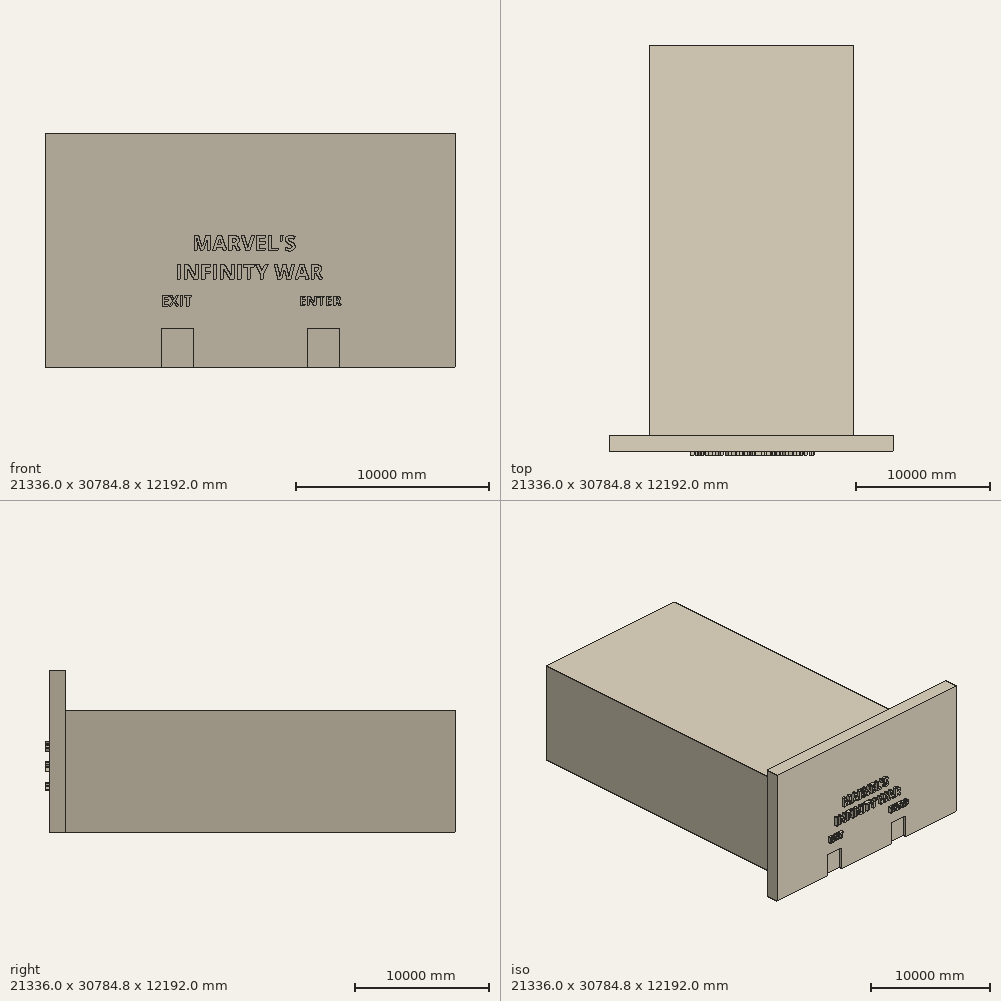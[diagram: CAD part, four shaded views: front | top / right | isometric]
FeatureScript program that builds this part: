
annotation { "Feature Type Name" : "Feature", "Feature Type Description" : "" }
export const myFeature = defineFeature(function(context is Context, id is Id, definition is map)
    precondition{}
    {
        {
            var Q0;
            Q0=qCreatedBy(makeId("Front.planeOp"),FACE);
            var sketch = newSketch(context, id + "F0", { "sketchPlane" : qUnion([Q0])});
            skLineSegment(sketch, "E0.bottom", {"start": v(-53.37, 9088.4) * mm, "end": v(15186.63, 9088.4) * mm});
            skLineSegment(sketch, "E0.top", {"start": v(-53.37, -55.6) * mm, "end": v(15186.63, -55.6) * mm});
            skLineSegment(sketch, "E0.left", {"start": v(-53.37, 9088.4) * mm, "end": v(-53.37, -55.6) * mm});
            skLineSegment(sketch, "E0.right", {"start": v(15186.63, 9088.4) * mm, "end": v(15186.63, -55.6) * mm});
            skSolve(sketch);
        }
        {
            var Q0;
            Q0=makeQuery(id+"F0.imprint","IMPRINT",FACE,{"disambiguationData":[TD([[makeQuery(id+"F0.imprint","IMPRINT",EDGE,{"derivedFrom":sQuery(id+"F0.wireOp",EDGE,"E0.bottom")}),-1.0]])]});
            extrude(context, id + "F1", {"entities" : qUnion([Q0]), "depth" : 30480 * mm, "offsetDistance" : 25 * mm});
        }
        {
            var Q0;
            Q0=makeQuery(id+"F1.opExtrude","SWEPT_FACE",FACE,{"disambiguationData":[OSD([sQuery(id+"F0.wireOp",EDGE,"E0.bottom")])]});
            var sketch = newSketch(context, id + "F2", { "sketchPlane" : qUnion([Q0])});
            skLineSegment(sketch, "E1.bottom", {"start": v(-53.37, -30480) * mm, "end": v(15186.63, -30480) * mm});
            skLineSegment(sketch, "E1.top", {"start": v(-53.37, -29276.97) * mm, "end": v(15186.63, -29276.97) * mm});
            skLineSegment(sketch, "E1.left", {"start": v(-53.37, -30480) * mm, "end": v(-53.37, -29276.97) * mm});
            skLineSegment(sketch, "E1.right", {"start": v(15186.63, -30480) * mm, "end": v(15186.63, -29276.97) * mm});
            skSolve(sketch);
        }
        {
            var Q0;
            Q0=makeQuery(id+"F2.imprint","IMPRINT",FACE,{"disambiguationData":[TD([[makeQuery(id+"F2.imprint","IMPRINT",EDGE,{"derivedFrom":sQuery(id+"F2.wireOp",EDGE,"E1.bottom")}),1.0]])]});
            extrude(context, id + "F3", {"entities" : qUnion([Q0]), "operationType" : NewBodyOperationType.ADD, "depth" : 3048 * mm, "offsetDistance" : 30.48 * mm});
        }
        {
            var Q0;
            Q0=makeQuery(id+"F3.boolean.opBoolean","MERGE",FACE,{"derivedFrom":[makeQuery(id+"F1.opExtrude","CAP_FACE",FACE,{"disambiguationData":[OSD([sQuery(id+"F0.wireOp",EDGE,"E0.bottom"),sQuery(id+"F0.wireOp",EDGE,"E0.top"),sQuery(id+"F0.wireOp",EDGE,"E0.left"),sQuery(id+"F0.wireOp",EDGE,"E0.right")])],"isStart":false}),makeQuery(id+"F3.opExtrude","SWEPT_FACE",FACE,{"disambiguationData":[OSD([sQuery(id+"F2.wireOp",EDGE,"E1.bottom")])]})]});
            var sketch = newSketch(context, id + "F4", { "sketchPlane" : qUnion([Q0])});
            skLineSegment(sketch, "E2", {"start": v(-53.37, -55.6) * mm, "end": v(3756.63, -55.6) * mm});
            skLineSegment(sketch, "E3", {"start": v(3756.63, -55.6) * mm, "end": v(7566.63, -55.6) * mm});
            skLineSegment(sketch, "E4", {"start": v(7566.63, -55.6) * mm, "end": v(11376.63, -55.6) * mm});
            skLineSegment(sketch, "E5", {"start": v(11376.63, -55.6) * mm, "end": v(15186.63, -55.6) * mm});
            skLineSegment(sketch, "E6", {"start": v(3756.63, -55.6) * mm, "end": v(3756.63, 1986.56) * mm});
            skLineSegment(sketch, "E7", {"start": v(11376.63, -55.6) * mm, "end": v(11376.63, 1986.56) * mm});
            skLineSegment(sketch, "E8", {"start": v(11376.63, 1986.56) * mm, "end": v(12199.6, 1986.56) * mm});
            skLineSegment(sketch, "E9", {"start": v(11376.63, 1986.56) * mm, "end": v(10553.67, 1986.56) * mm});
            skLineSegment(sketch, "E10", {"start": v(3756.63, 1986.56) * mm, "end": v(4579.6, 1986.56) * mm});
            skLineSegment(sketch, "E11", {"start": v(3756.63, 1986.56) * mm, "end": v(2933.67, 1986.56) * mm});
            skLineSegment(sketch, "E12", {"start": v(2933.67, 1986.56) * mm, "end": v(2933.67, -55.6) * mm});
            skPoint(sketch, "E12.endSnap0", {"position": v(1851.63, -55.6) * mm});
            skLineSegment(sketch, "E13", {"start": v(4579.6, 1986.56) * mm, "end": v(4579.6, -55.6) * mm});
            skLineSegment(sketch, "E14", {"start": v(10553.67, 1986.56) * mm, "end": v(10553.67, -55.6) * mm});
            skLineSegment(sketch, "E15", {"start": v(12199.6, 1986.56) * mm, "end": v(12199.6, -55.6) * mm});
            skSolve(sketch);
        }
        {
            var Q0;
            {var subQ0=sQuery(id+"F4.wireOp",EDGE,"E6");Q0=makeQuery(id+"F4.imprint","IMPRINT",FACE,{"disambiguationData":[TD([[makeQuery(id+"F4.imprint","IMPRINT",EDGE,{"derivedFrom":subQ0}),1.0]])]});}
            var Q1;
            {var subQ0=sQuery(id+"F4.wireOp",EDGE,"E6");Q1=makeQuery(id+"F4.imprint","IMPRINT",FACE,{"disambiguationData":[TD([[makeQuery(id+"F4.imprint","IMPRINT",EDGE,{"derivedFrom":subQ0}),-1.0]])]});}
            var Q2;
            {var subQ0=sQuery(id+"F4.wireOp",EDGE,"E7");Q2=makeQuery(id+"F4.imprint","IMPRINT",FACE,{"disambiguationData":[TD([[makeQuery(id+"F4.imprint","IMPRINT",EDGE,{"derivedFrom":subQ0}),1.0]])]});}
            var Q3;
            {var subQ0=sQuery(id+"F4.wireOp",EDGE,"E7");Q3=makeQuery(id+"F4.imprint","IMPRINT",FACE,{"disambiguationData":[TD([[makeQuery(id+"F4.imprint","IMPRINT",EDGE,{"derivedFrom":subQ0}),-1.0]])]});}
            extrude(context, id + "F5", {"entities" : qUnion([Q0, Q1, Q2, Q3]), "operationType" : NewBodyOperationType.REMOVE, "oppositeDirection" : true, "depth" : 304.8 * mm, "offsetDistance" : 30.48 * mm});
        }
        {
            var Q0;
            Q0=makeQuery(id+"F3.boolean.opBoolean","MERGE",FACE,{"derivedFrom":[makeQuery(id+"F1.opExtrude","CAP_FACE",FACE,{"disambiguationData":[OSD([sQuery(id+"F0.wireOp",EDGE,"E0.bottom"),sQuery(id+"F0.wireOp",EDGE,"E0.top"),sQuery(id+"F0.wireOp",EDGE,"E0.left"),sQuery(id+"F0.wireOp",EDGE,"E0.right")])],"isStart":false}),makeQuery(id+"F3.opExtrude","SWEPT_FACE",FACE,{"disambiguationData":[OSD([sQuery(id+"F2.wireOp",EDGE,"E1.bottom")])]})]});
            var sketch = newSketch(context, id + "F6", { "sketchPlane" : qUnion([Q0])});
            skLineSegment(sketch, "E16.bottom", {"start": v(2933.67, 3142.1) * mm, "end": v(4579.6, 3142.1) * mm});
            skLineSegment(sketch, "E16.right", {"start": v(4579.6, 3142.1) * mm, "end": v(4579.6, 3685.2) * mm});
            skSolve(sketch);
        }
        {
            var Q0;
            {var subQ1=sQuery(id+"F2.wireOp",EDGE,"E1.bottom");Q0=makeQuery(id+"F6.imprint","IMPRINT",FACE,{"disambiguationData":[TD([[makeQuery(id+"F6.imprint","IMPRINT",EDGE,{"derivedFrom":makeQuery(id+"F3.opExtrude","CAP_EDGE",EDGE,{"disambiguationData":[OSD([subQ1])],"isStart":false})}),-1.0]])]});}
            var sketch = newSketch(context, id + "F7", { "sketchPlane" : qUnion([Q0])});
            skText(sketch, "E17", { "text": "EXIT", "fontName": "OpenSans-Bold.ttf"});
            const initialGuessF7  = {"E17": [2.92453, 3.14832, 1, 0, 0.54104]};
            skSetInitialGuess(sketch, initialGuessF7);
            skSolve(sketch);
        }
        {
            var Q0;
            Q0 = qSketchRegion(id + "F7", true);
            extrude(context, id + "F8", {"entities" : qUnion([Q0]), "operationType" : NewBodyOperationType.ADD, "depth" : 304.8 * mm, "offsetDistance" : 30.48 * mm});
        }
        {
            var Q0;
            {var subQ1=sQuery(id+"F2.wireOp",EDGE,"E1.bottom");Q0=makeQuery(id+"F6.imprint","IMPRINT",FACE,{"disambiguationData":[TD([[makeQuery(id+"F6.imprint","IMPRINT",EDGE,{"derivedFrom":makeQuery(id+"F3.opExtrude","CAP_EDGE",EDGE,{"disambiguationData":[OSD([subQ1])],"isStart":false})}),-1.0]])]});}
            var sketch = newSketch(context, id + "F9", { "sketchPlane" : qUnion([Q0])});
            skText(sketch, "E18", { "text": "ENTER", "fontName": "OpenSans-Bold.ttf"});
            const initialGuessF9  = {"E18": [10.0868, 3.16649, 1, 0, 0.5048]};
            skSetInitialGuess(sketch, initialGuessF9);
            skSolve(sketch);
        }
        {
            var Q0;
            Q0 = qSketchRegion(id + "F9", true);
            extrude(context, id + "F10", {"entities" : qUnion([Q0]), "operationType" : NewBodyOperationType.ADD, "depth" : 304.8 * mm, "offsetDistance" : 30.48 * mm});
        }
        {
            var Q0;
            Q0=makeQuery(id+"F3.boolean.opBoolean","MERGE",FACE,{"derivedFrom":[makeQuery(id+"F1.opExtrude","SWEPT_FACE",FACE,{"disambiguationData":[OSD([sQuery(id+"F0.wireOp",EDGE,"E0.right")])]}),makeQuery(id+"F3.opExtrude","SWEPT_FACE",FACE,{"disambiguationData":[OSD([sQuery(id+"F2.wireOp",EDGE,"E1.right")])]})]});
            var sketch = newSketch(context, id + "F11", { "sketchPlane" : qUnion([Q0])});
            skLineSegment(sketch, "E19", {"start": v(-29276.97, 9088.4) * mm, "end": v(-29276.97, -55.6) * mm});
            skSolve(sketch);
        }
        {
            var Q0;
            {var subQ3=sQuery(id+"F11.wireOp",EDGE,"E19");Q0=makeQuery(id+"F11.imprint","IMPRINT",FACE,{"disambiguationData":[TD([[makeQuery(id+"F11.imprint","IMPRINT",EDGE,{"derivedFrom":subQ3}),-1.0]])]});}
            extrude(context, id + "F12", {"entities" : qUnion([Q0]), "operationType" : NewBodyOperationType.ADD, "depth" : 3048 * mm, "offsetDistance" : 30.48 * mm});
        }
        {
            var Q0;
            Q0=makeQuery(id+"F3.boolean.opBoolean","MERGE",FACE,{"derivedFrom":[makeQuery(id+"F1.opExtrude","SWEPT_FACE",FACE,{"disambiguationData":[OSD([sQuery(id+"F0.wireOp",EDGE,"E0.left")])]}),makeQuery(id+"F3.opExtrude","SWEPT_FACE",FACE,{"disambiguationData":[OSD([sQuery(id+"F2.wireOp",EDGE,"E1.left")])]})]});
            var sketch = newSketch(context, id + "F13", { "sketchPlane" : qUnion([Q0])});
            skLineSegment(sketch, "E20", {"start": v(29276.97, 9088.4) * mm, "end": v(29276.97, -55.6) * mm});
            skSolve(sketch);
        }
        {
            var Q0;
            {var subQ3=sQuery(id+"F13.wireOp",EDGE,"E20");Q0=makeQuery(id+"F13.imprint","IMPRINT",FACE,{"disambiguationData":[TD([[makeQuery(id+"F13.imprint","IMPRINT",EDGE,{"derivedFrom":subQ3}),1.0]])]});}
            extrude(context, id + "F14", {"entities" : qUnion([Q0]), "operationType" : NewBodyOperationType.ADD, "depth" : 3048 * mm, "offsetDistance" : 30.48 * mm});
        }
        {
            var Q0;
            {var subQ1=sQuery(id+"F2.wireOp",EDGE,"E1.bottom");Q0=makeQuery(id+"F6.imprint","IMPRINT",FACE,{"disambiguationData":[TD([[makeQuery(id+"F6.imprint","IMPRINT",EDGE,{"derivedFrom":makeQuery(id+"F3.opExtrude","CAP_EDGE",EDGE,{"disambiguationData":[OSD([subQ1])],"isStart":false})}),-1.0]])]});}
            var sketch = newSketch(context, id + "F15", { "sketchPlane" : qUnion([Q0])});
            skText(sketch, "E21", { "text": "   MARVEL\'S \nINFINITY WAR", "fontName": "OpenSans-Bold.ttf"});
            const initialGuessF15  = {"E21": [3.67678, 6.01989, 1, 0, 0.79635]};
            skSetInitialGuess(sketch, initialGuessF15);
            skSolve(sketch);
        }
        {
            var Q0;
            Q0 = qSketchRegion(id + "F15", true);
            extrude(context, id + "F16", {"entities" : qUnion([Q0]), "operationType" : NewBodyOperationType.ADD, "depth" : 304.8 * mm, "offsetDistance" : 30.48 * mm});
        }
    });
